# Revit family: Soap Holder-Wall-Dorf Kip1
name_source: partatom
category: Specialty Equipment
revit_build: Autodesk Revit 2014 (Build: 20131024_2115(x64)
units: mm (PartAtom-declared; Revit-internal decimal feet)

## types (1)
- Standard
    Assembly Code = C1030200
    Cost = 0 $
    Default Elevation = 1000 mm  [stored 3.28084 ft]
    Description = The Dorf Kip collection, complete with a full range of bathroom accessories and mixer taps offers a streamlined design, versatility and lasting quality.
    Glazing = Glass-Clear-Caroma
    Height_ANZRS = 53 mm
    Length_ANZRS = 109 mm  [stored 0.357612 ft]
    Manufacturer = GWA Bathrooms & Kitchens
    Material_ANZRS = Metal-Chrome-Caroma
    Model = 872890C
    ModifiedIssue_ANZRS = 20150421.01 $
    Type Comments = Caroma Kip Soap Dish
    URL = http://specify.caroma.com.au
    Width_ANZRS = 124 mm

note: [stored X ft] marks values corroborated as IEEE doubles in the binary element streams (Revit-internal decimal feet)

## geometry (parser evidence)
native form markers: Blend x8, Sweep x1
no freeform markers — native parametric forms only
